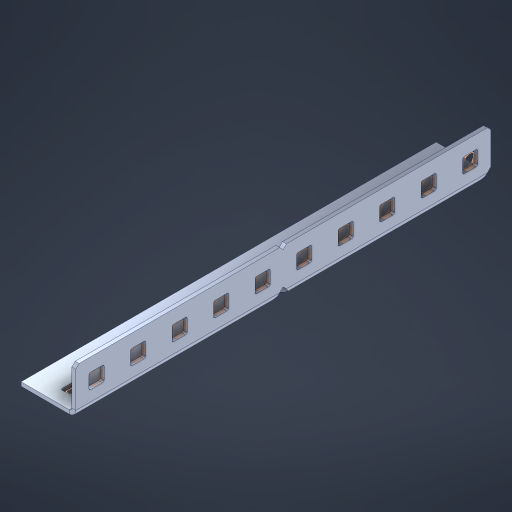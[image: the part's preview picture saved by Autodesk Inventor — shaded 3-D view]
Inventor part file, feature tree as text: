
AUTODESK INVENTOR PART (.ipt)
format: ipt  version: 2023 (Build 270158000, 158)  size: 561,152 bytes
history: native  units: in
note: dims shown in document units (in); Inventor stores cm internally (conversion verified against a paired STEP export)
features: other x25, extrude x19, sheet_metal_op x10, sketch x8, mirror x1, pattern_linear x1, chamfer x1
ambient origin geometry x8: Origin, YZ Plane, XZ Plane, XY Plane, X Axis, Y Axis, Z Axis, Center Point
bodies: Solid1 (feature_tree), Body (feature_tree)
feature tree (65):
  other  "Flange Pattern Plane"
  sheet_metal_op  "Flange Pattern"
  sheet_metal_op  "Body Pattern"
  other  "Arc Length"
  mirror  "Notch Mirror"
  pattern_linear  "Notch Pattern"  Spacing1=0.1875in  [1 undecoded]
  chamfer  "End Chamfer"
  extrude  "Half Cut"  Depth=0.0469in
  sketch  "Sketch1"  dims[d0=2.5in]
  other  "Plate1"
  sketch  "Sketch2"  dims[d1=5.0in]
  other  "Plate2"
  sheet_metal_op  "Bend1"
  sheet_metal_op  "Corner1"
  sketch  "Sketch3"  dims[d2=0.0469in]
  other  "Flange Pattern Sketch"
  sketch  "Sketch7"  dims[d3=0.0469in]
  other  "Srf1"
  other  "Srf2"
  sketch  "Sketch8"  dims[d4=0.0234in]
  sketch  "Sketch9"  dims[d5=0.0938in]
  other  "Srf91"
  sheet_metal_op  "Body Pattern Sketch"
  other  "Srf92"
  sketch  "Sketch13"  dims[d6=0.0469in]
  sketch  "Sketch14"  dims[d7=0.5in d8=90.0deg d9=0.0312in d10=0.1875in d11=0.0469in d12=0.0469in d16=0.182in d17=0.02in d18=0.0469in d19=0.0in d20=0.25in d21=0.25in d46=0.172in d47=1.0in d48=0.0in d49=0.182in d50=0.02in d51=0.25in d52=0.25in d53=0.0469in d54=0.0in d55=0.172in d56=1.0in d57=0.0in d60=3.937in d62=0.5in d63=0.3937in d65=0.5in d85=0.1227in d86=0.1659in d88=0.04in d89=0.0469in d90=0.0in d91=0.04in d92=0.0491in d95=2.5in d96=0.04in d97=0.25in d98=45.0deg d101=0.0in d102=2.497in d131=0.5in d132=3.937in d134=0.5in d139=0.5in]
  other  "Srf856"
  other  "Srf1310"
  other  "Srf1311"
  other  "Srf1312"
  other  "Srf1376"
  other  "Srf1377"
  other  "Srf1728"
  other  "Srf1755"
  other  "Srf1878"
  other  "Srf1879"
  other  "Srf1880"
  other  "Srf1881"
  other  "Srf1942"
  other  "Srf1943"
  other  "Srf1944"
  other  "Srf1945"
  sheet_metal_op  "Flange Stamp"
  sheet_metal_op  "Flange Circle"
  sheet_metal_op  "Body Stamp"
  sheet_metal_op  "Body Circle"
  sheet_metal_op  "Notch"
  extrude  "ExtrusionSrf2"  Depth=0.0469in
  extrude  "ExtrusionSrf92"  Depth=0.5in
  extrude  "ExtrusionSrf856"  Depth=0.02in
  extrude  "ExtrusionSrf1310"  Depth=0.0469in
  extrude  "ExtrusionSrf1311"  TaperAngle=0.0deg  [1 undecoded]
  extrude  "ExtrusionSrf1312"  Depth=0.5in
  extrude  "ExtrusionSrf1376"  Depth=0.5in
  extrude  "ExtrusionSrf1377"  Depth=0.5in
  extrude  "ExtrusionSrf1728"  Depth=0.5in TaperAngle=0.0deg
  extrude  "ExtrusionSrf1755"  Depth=0.5in
  extrude  "ExtrusionSrf1878"  Depth=0.02in
  extrude  "ExtrusionSrf1879"  Depth=0.5in
  extrude  "ExtrusionSrf1880"  Depth=0.5in
  extrude  "ExtrusionSrf1881"  Depth=0.0469in
  extrude  "ExtrusionSrf1942"  TaperAngle=0.0deg  [1 undecoded]
  extrude  "ExtrusionSrf1943"  Depth=0.5in
  extrude  "ExtrusionSrf1944"  Depth=0.5in TaperAngle=0.0deg
  extrude  "ExtrusionSrf1945"  Depth=0.5in
note: 3 required parameter values undecoded (feature->parameter linkage not recoverable at this tier; creation-order binding heuristic only, values carry confidence <= 0.55)
